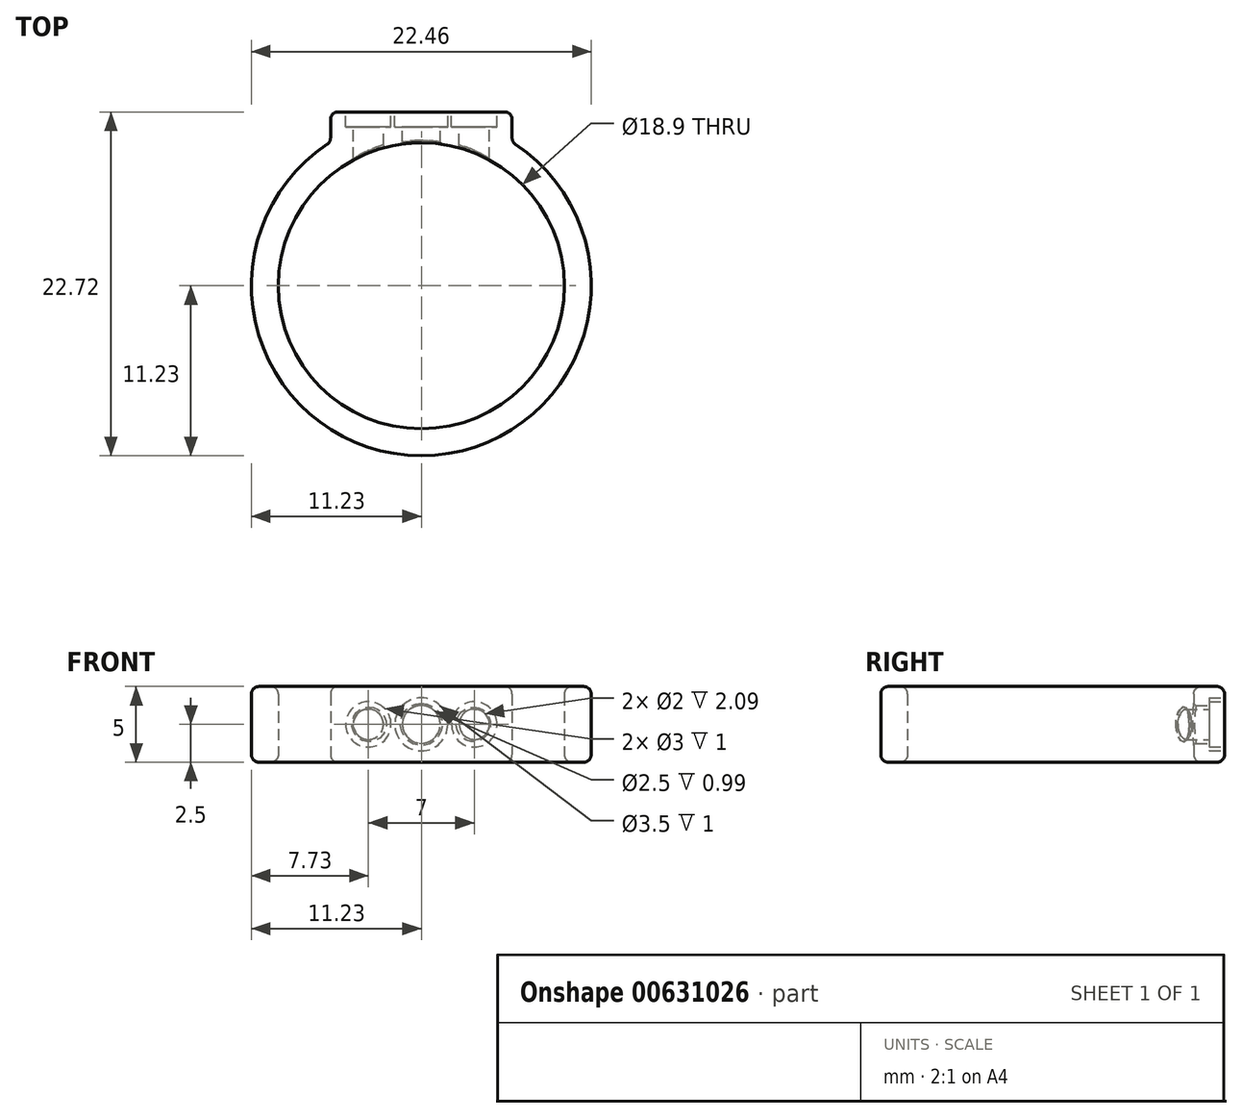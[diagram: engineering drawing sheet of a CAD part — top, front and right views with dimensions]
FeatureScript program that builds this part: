
annotation { "Feature Type Name" : "Feature", "Feature Type Description" : "" }
export const myFeature = defineFeature(function(context is Context, id is Id, definition is map)
    precondition{}
    {
        {
            var Q0;
            Q0=qCreatedBy(makeId("Top.planeOp"),FACE);
            var sketch = newSketch(context, id + "F0", { "sketchPlane" : qUnion([Q0])});
            skCircle(sketch, "E0", {"center": v(0, 0) * mm, "radius": 9.45 * mm});
            skArc(sketch, "E1", {"start": v(-6.22, 9.34) * mm, "mid": v(0, -11.23) * mm, "end": v(6.22, 9.34) * mm});
            skLineSegment(sketch, "E2.top", {"start": v(-5.5, 11.49) * mm, "end": v(5.5, 11.49) * mm});
            skLineSegment(sketch, "E2.left", {"start": v(-6, 9.76) * mm, "end": v(-6, 10.99) * mm});
            skLineSegment(sketch, "E2.right", {"start": v(6, 9.76) * mm, "end": v(6, 10.99) * mm});
            skPoint(sketch, "E3.visualSharp", {"position": v(-6, 9.49) * mm});
            skArc(sketch, "E3.filletArc", {"start": v(-6.22, 9.34) * mm, "mid": v(-6.06, 9.52) * mm, "end": v(-6, 9.76) * mm});
            skPoint(sketch, "E4.visualSharp", {"position": v(6, 9.49) * mm});
            skArc(sketch, "E4.filletArc", {"start": v(6, 9.76) * mm, "mid": v(6.06, 9.52) * mm, "end": v(6.22, 9.34) * mm});
            skPoint(sketch, "E5.visualSharp", {"position": v(-6, 11.49) * mm});
            skArc(sketch, "E5.filletArc", {"start": v(-5.5, 11.49) * mm, "mid": v(-5.85, 11.34) * mm, "end": v(-6, 10.99) * mm});
            skPoint(sketch, "E6.visualSharp", {"position": v(6, 11.49) * mm});
            skArc(sketch, "E6.filletArc", {"start": v(6, 10.99) * mm, "mid": v(5.85, 11.34) * mm, "end": v(5.5, 11.49) * mm});
            skSolve(sketch);
        }
        {
            var Q0;
            Q0=makeQuery(id+"F0.imprint","IMPRINT",FACE,{"disambiguationData":[TD([[makeQuery(id+"F0.imprint","IMPRINT",EDGE,{"derivedFrom":sQuery(id+"F0.wireOp",EDGE,"E0")}),-1.0]])]});
            extrude(context, id + "F1", {"entities" : qUnion([Q0]), "depth" : 5 * mm, "offsetDistance" : 25 * mm});
        }
        {
            var Q0;
            Q0=makeQuery(id+"F1.opExtrude","CAP_EDGE",EDGE,{"disambiguationData":[OSD([sQuery(id+"F0.wireOp",EDGE,"E0")])],"isStart":false});
            var Q1;
            Q1=makeQuery(id+"F1.opExtrude","CAP_EDGE",EDGE,{"disambiguationData":[OSD([sQuery(id+"F0.wireOp",EDGE,"E1")])],"isStart":false});
            var Q2;
            Q2=makeQuery(id+"F1.opExtrude","CAP_EDGE",EDGE,{"disambiguationData":[OSD([sQuery(id+"F0.wireOp",EDGE,"E1")])],"isStart":true});
            var Q3;
            Q3=makeQuery(id+"F1.opExtrude","CAP_EDGE",EDGE,{"disambiguationData":[OSD([sQuery(id+"F0.wireOp",EDGE,"E0")])],"isStart":true});
            fillet(context, id + "F2", {"entities" : qUnion([Q0, Q1, Q2, Q3]), "radius" : 0.5 * mm, "tangentPropagation" : true, "allowEdgeOverflow" : false});
        }
        {
            var Q0;
            Q0=makeQuery(id+"F1.opExtrude","SWEPT_FACE",FACE,{"disambiguationData":[OSD([sQuery(id+"F0.wireOp",EDGE,"E2.top")])]});
            var sketch = newSketch(context, id + "F3", { "sketchPlane" : qUnion([Q0])});
            skCircle(sketch, "E7", {"center": v(0, 2.5) * mm, "radius": 1.25 * mm});
            skCircle(sketch, "E8", {"center": v(-3.5, 2.5) * mm, "radius": 1 * mm});
            skCircle(sketch, "E9", {"center": v(3.5, 2.5) * mm, "radius": 1 * mm});
            skLineSegment(sketch, "E10", {"start": v(0, 4.5) * mm, "end": v(0, 0.5) * mm});
            skLineSegment(sketch, "E11", {"start": v(-5.5, 2.5) * mm, "end": v(5.5, 2.5) * mm});
            skSolve(sketch);
        }
        {
            var Q0;
            Q0 = qSketchRegion(id + "F3", true);
            extrude(context, id + "F4", {"entities" : qUnion([Q0]), "operationType" : NewBodyOperationType.REMOVE, "oppositeDirection" : true, "depth" : 5 * mm, "offsetDistance" : 25 * mm});
        }
        {
            var Q0;
            Q0=makeQuery(id+"F1.opExtrude","SWEPT_FACE",FACE,{"disambiguationData":[OSD([sQuery(id+"F0.wireOp",EDGE,"E2.top")])]});
            var sketch = newSketch(context, id + "F5", { "sketchPlane" : qUnion([Q0])});
            skCircle(sketch, "E12", {"center": v(0, 2.5) * mm, "radius": 1.75 * mm});
            skCircle(sketch, "E13", {"center": v(-3.5, 2.5) * mm, "radius": 1.5 * mm});
            skCircle(sketch, "E14", {"center": v(3.5, 2.5) * mm, "radius": 1.5 * mm});
            skSolve(sketch);
        }
        {
            var Q0;
            Q0 = qSketchRegion(id + "F5", true);
            extrude(context, id + "F6", {"entities" : qUnion([Q0]), "operationType" : NewBodyOperationType.REMOVE, "oppositeDirection" : true, "depth" : 1 * mm, "offsetDistance" : 25 * mm});
        }
        {
            var Q0;
            Q0=makeQuery(id+"F4.boolean.opBoolean","INTERSECT",EDGE,{"derivedFrom":[makeQuery(id+"F1.opExtrude","SWEPT_FACE",FACE,{"disambiguationData":[OSD([sQuery(id+"F0.wireOp",EDGE,"E0")])]}),makeQuery(id+"F4.opExtrude","SWEPT_FACE",FACE,{"disambiguationData":[OSD([sQuery(id+"F3.wireOp",EDGE,"E9")])]})]});
            var Q1;
            Q1=makeQuery(id+"F4.boolean.opBoolean","INTERSECT",EDGE,{"derivedFrom":[makeQuery(id+"F1.opExtrude","SWEPT_FACE",FACE,{"disambiguationData":[OSD([sQuery(id+"F0.wireOp",EDGE,"E0")])]}),makeQuery(id+"F4.opExtrude","SWEPT_FACE",FACE,{"disambiguationData":[OSD([sQuery(id+"F3.wireOp",EDGE,"E7")])]})]});
            var Q2;
            Q2=makeQuery(id+"F4.boolean.opBoolean","INTERSECT",EDGE,{"derivedFrom":[makeQuery(id+"F1.opExtrude","SWEPT_FACE",FACE,{"disambiguationData":[OSD([sQuery(id+"F0.wireOp",EDGE,"E0")])]}),makeQuery(id+"F4.opExtrude","SWEPT_FACE",FACE,{"disambiguationData":[OSD([sQuery(id+"F3.wireOp",EDGE,"E8")])]})]});
            fillet(context, id + "F7", {"entities" : qUnion([Q0, Q1, Q2]), "radius" : 0.15 * mm, "tangentPropagation" : true, "allowEdgeOverflow" : false});
        }
    });
